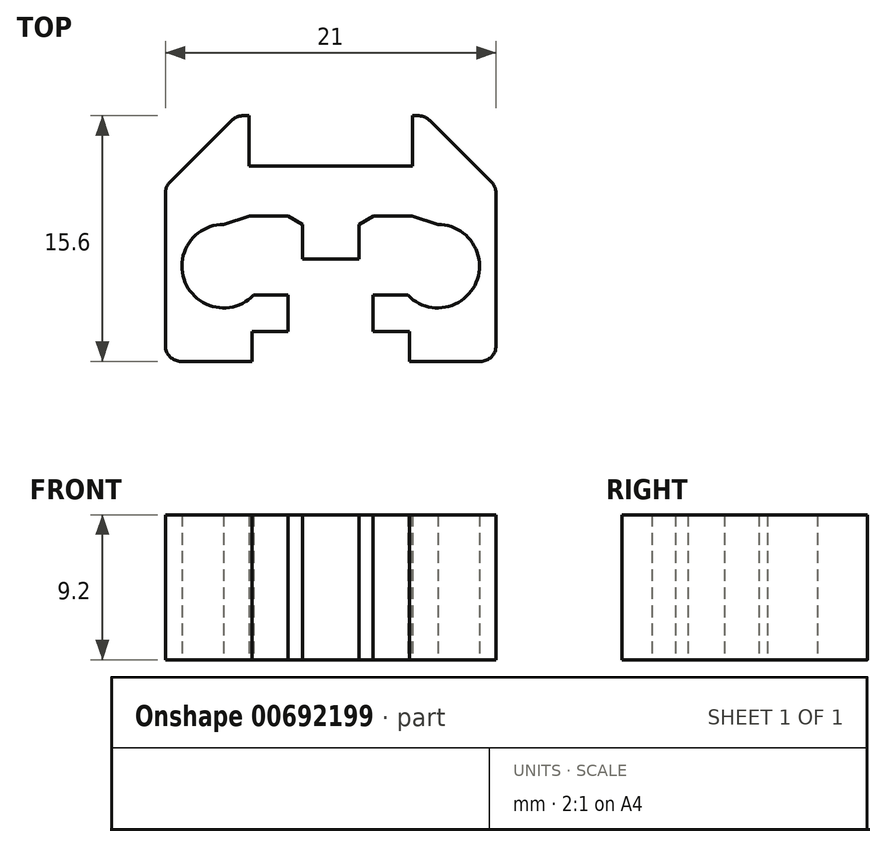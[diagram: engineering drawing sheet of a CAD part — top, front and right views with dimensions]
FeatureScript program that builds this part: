
annotation { "Feature Type Name" : "Feature", "Feature Type Description" : "" }
export const myFeature = defineFeature(function(context is Context, id is Id, definition is map)
    precondition{}
    {
        {
            var Q0;
            Q0=qCreatedBy(makeId("Top.planeOp"),FACE);
            var sketch = newSketch(context, id + "F0", { "sketchPlane" : qUnion([Q0])});
            skLineSegment(sketch, "E0.bottom", {"start": v(-10.5, 0) * mm, "end": v(10.5, 0) * mm});
            skLineSegment(sketch, "E0.top", {"start": v(-10.5, 18) * mm, "end": v(10.5, 18) * mm});
            skLineSegment(sketch, "E0.left", {"start": v(-10.5, 0) * mm, "end": v(-10.5, 18) * mm});
            skLineSegment(sketch, "E0.right", {"start": v(10.5, 0) * mm, "end": v(10.5, 18) * mm});
            skLineSegment(sketch, "E1", {"start": v(0, 0) * mm, "end": v(0, 18) * mm, "construction": true});
            skLineSegment(sketch, "E2", {"start": v(0, 16.8) * mm, "end": v(-5.2, 16.8) * mm});
            skLineSegment(sketch, "E3", {"start": v(-5.2, 16.8) * mm, "end": v(-5.2, 13.6) * mm});
            skLineSegment(sketch, "E4", {"start": v(-5.2, 13.6) * mm, "end": v(0, 13.6) * mm});
            skLineSegment(sketch, "E5", {"start": v(0, 7.7) * mm, "end": v(-1.8, 7.7) * mm});
            skLineSegment(sketch, "E6", {"start": v(-1.8, 7.7) * mm, "end": v(-1.8, 9.9) * mm});
            skLineSegment(sketch, "E7", {"start": v(-1.8, 9.9) * mm, "end": v(-6.8, 9.9) * mm});
            skLineSegment(sketch, "E8", {"start": v(-6.8, 9.9) * mm, "end": v(-6.3, 5.4) * mm});
            skLineSegment(sketch, "E9", {"start": v(-6.3, 5.4) * mm, "end": v(-2.7, 5.4) * mm});
            skLineSegment(sketch, "E10", {"start": v(-2.7, 5.4) * mm, "end": v(-2.7, 3.1) * mm});
            skLineSegment(sketch, "E11", {"start": v(-4, 1.2) * mm, "end": v(-5, 1.2) * mm});
            skLineSegment(sketch, "E12", {"start": v(-5, 1.2) * mm, "end": v(-5, 3.1) * mm});
            skLineSegment(sketch, "E13", {"start": v(-5, 3.1) * mm, "end": v(-2.7, 3.1) * mm});
            skLineSegment(sketch, "E14.MirrorCS", {"start": v(2.7, 3.1) * mm, "end": v(2.7, 3.1) * mm});
            skLineSegment(sketch, "E15.MirrorCS", {"start": v(5, 3.1) * mm, "end": v(2.7, 3.1) * mm});
            skLineSegment(sketch, "E16.MirrorCS", {"start": v(6.8, 9.9) * mm, "end": v(6.3, 5.4) * mm});
            skLineSegment(sketch, "E17.MirrorCS", {"start": v(5, 1.2) * mm, "end": v(5, 3.1) * mm});
            skLineSegment(sketch, "E18.MirrorCS", {"start": v(2.7, 5.4) * mm, "end": v(2.7, 3.1) * mm});
            skLineSegment(sketch, "E19.MirrorCS", {"start": v(1.8, 9.9) * mm, "end": v(6.8, 9.9) * mm});
            skLineSegment(sketch, "E20.MirrorCS", {"start": v(1.8, 7.7) * mm, "end": v(1.8, 9.9) * mm});
            skLineSegment(sketch, "E21.MirrorCS", {"start": v(4, 1.2) * mm, "end": v(5, 1.2) * mm});
            skLineSegment(sketch, "E22.MirrorCS", {"start": v(6.3, 5.4) * mm, "end": v(2.7, 5.4) * mm});
            skLineSegment(sketch, "E23.MirrorCS", {"start": v(0, 7.7) * mm, "end": v(1.8, 7.7) * mm});
            skLineSegment(sketch, "E24.MirrorCS", {"start": v(5.2, 16.8) * mm, "end": v(5.2, 13.6) * mm});
            skLineSegment(sketch, "E25.MirrorCS", {"start": v(5.2, 13.6) * mm, "end": v(0, 13.6) * mm});
            skLineSegment(sketch, "E26.MirrorCS", {"start": v(0, 16.8) * mm, "end": v(5.2, 16.8) * mm});
            skLineSegment(sketch, "E27", {"start": v(-2.7, 3.1) * mm, "end": v(0, 3.1) * mm});
            skLineSegment(sketch, "E28.MirrorCS", {"start": v(2.7, 3.1) * mm, "end": v(0, 3.1) * mm});
            skLineSegment(sketch, "E29", {"start": v(-4, 1.2) * mm, "end": v(0, 1.2) * mm});
            skLineSegment(sketch, "E30.MirrorCS", {"start": v(4, 1.2) * mm, "end": v(0, 1.2) * mm});
            skLineSegment(sketch, "E31", {"start": v(-5.2, 16.8) * mm, "end": v(-10.5, 16.8) * mm});
            skLineSegment(sketch, "E32.MirrorCS", {"start": v(5.2, 16.8) * mm, "end": v(10.5, 16.8) * mm});
            skArc(sketch, "E33", {"start": v(-6.8, 9.9) * mm, "mid": v(-9.24, 6.22) * mm, "end": v(-4.9, 5.4) * mm});
            skArc(sketch, "E34.MirrorCS", {"start": v(6.8, 9.9) * mm, "mid": v(9.24, 6.22) * mm, "end": v(4.9, 5.4) * mm});
            skLineSegment(sketch, "E35", {"start": v(-5, 1.2) * mm, "end": v(-10.5, 1.2) * mm});
            skLineSegment(sketch, "E36.MirrorCS", {"start": v(5, 1.2) * mm, "end": v(10.5, 1.2) * mm});
            skLineSegment(sketch, "E37", {"start": v(-5, 1.2) * mm, "end": v(-5, 0) * mm});
            skLineSegment(sketch, "E38.MirrorCS", {"start": v(5, 1.2) * mm, "end": v(5, 0) * mm});
            skLineSegment(sketch, "E39", {"start": v(-10.5, 0.9) * mm, "end": v(10.5, 0.9) * mm, "construction": true});
            skLineSegment(sketch, "E40", {"start": v(-6, 16.8) * mm, "end": v(-10.5, 12.3) * mm});
            skLineSegment(sketch, "E41", {"start": v(-6, 17.1) * mm, "end": v(-10.5, 12.6) * mm, "construction": true});
            skLineSegment(sketch, "E42", {"start": v(-10.8, 0.9) * mm, "end": v(-10.5, 0.9) * mm, "construction": true});
            skLineSegment(sketch, "E43", {"start": v(-10.5, 12.6) * mm, "end": v(-10.8, 12.3) * mm, "construction": true});
            skLineSegment(sketch, "E44", {"start": v(-10.8, 12.3) * mm, "end": v(-10.8, 0.9) * mm, "construction": true});
            skLineSegment(sketch, "E45", {"start": v(-6, 17.1) * mm, "end": v(0, 17.1) * mm, "construction": true});
            skLineSegment(sketch, "E46.MirrorCS", {"start": v(6, 16.8) * mm, "end": v(10.5, 12.3) * mm});
            skLineSegment(sketch, "E47", {"start": v(-1.8, 9.9) * mm, "end": v(-2.72, 10.44) * mm});
            skLineSegment(sketch, "E48", {"start": v(-2.72, 10.44) * mm, "end": v(-5.15, 10.44) * mm});
            skLineSegment(sketch, "E49", {"start": v(-5.15, 10.44) * mm, "end": v(-6.8, 9.9) * mm});
            skLineSegment(sketch, "E50.MirrorCS", {"start": v(1.8, 9.9) * mm, "end": v(2.72, 10.44) * mm});
            skLineSegment(sketch, "E51.MirrorCS", {"start": v(2.72, 10.44) * mm, "end": v(5.15, 10.44) * mm});
            skLineSegment(sketch, "E52.MirrorCS", {"start": v(5.15, 10.44) * mm, "end": v(6.8, 9.9) * mm});
            skSolve(sketch);
        }
        {
            var Q0;
            {var subQ3=sQuery(id+"F0.wireOp",EDGE,"E3");Q0=makeQuery(id+"F0.imprint","IMPRINT",FACE,{"disambiguationData":[TD([[makeQuery(id+"F0.imprint","IMPRINT",EDGE,{"derivedFrom":subQ3}),-1.0]])]});}
            extrude(context, id + "F1", {"entities" : qUnion([Q0]), "depth" : 9.2 * mm, "offsetDistance" : 25 * mm});
        }
        {
            var Q0;
            Q0=makeQuery(id+"F1.opExtrude","SWEPT_EDGE",EDGE,{"disambiguationData":[OSD([sQuery(id+"F0.wireOp",EDGE,"E0.left"),sQuery(id+"F0.wireOp",EDGE,"E35")])]});
            var Q1;
            Q1=makeQuery(id+"F1.opExtrude","SWEPT_EDGE",EDGE,{"disambiguationData":[OSD([sQuery(id+"F0.wireOp",EDGE,"E0.right"),sQuery(id+"F0.wireOp",EDGE,"E36.MirrorCS")])]});
            var Q2;
            Q2=makeQuery(id+"F1.opExtrude","SWEPT_EDGE",EDGE,{"disambiguationData":[OSD([sQuery(id+"F0.wireOp",EDGE,"E0.right"),sQuery(id+"F0.wireOp",EDGE,"E46.MirrorCS")])]});
            var Q3;
            Q3=makeQuery(id+"F1.opExtrude","SWEPT_EDGE",EDGE,{"disambiguationData":[OSD([sQuery(id+"F0.wireOp",EDGE,"E32.MirrorCS"),sQuery(id+"F0.wireOp",EDGE,"E46.MirrorCS")])]});
            var Q4;
            Q4=makeQuery(id+"F1.opExtrude","SWEPT_EDGE",EDGE,{"disambiguationData":[OSD([sQuery(id+"F0.wireOp",EDGE,"E31"),sQuery(id+"F0.wireOp",EDGE,"E40")])]});
            var Q5;
            Q5=makeQuery(id+"F1.opExtrude","SWEPT_EDGE",EDGE,{"disambiguationData":[OSD([sQuery(id+"F0.wireOp",EDGE,"E0.left"),sQuery(id+"F0.wireOp",EDGE,"E40")])]});
            fillet(context, id + "F2", {"entities" : qUnion([Q0, Q1, Q2, Q3, Q4, Q5]), "radius" : 1 * mm, "tangentPropagation" : true, "allowEdgeOverflow" : false});
        }
    });
